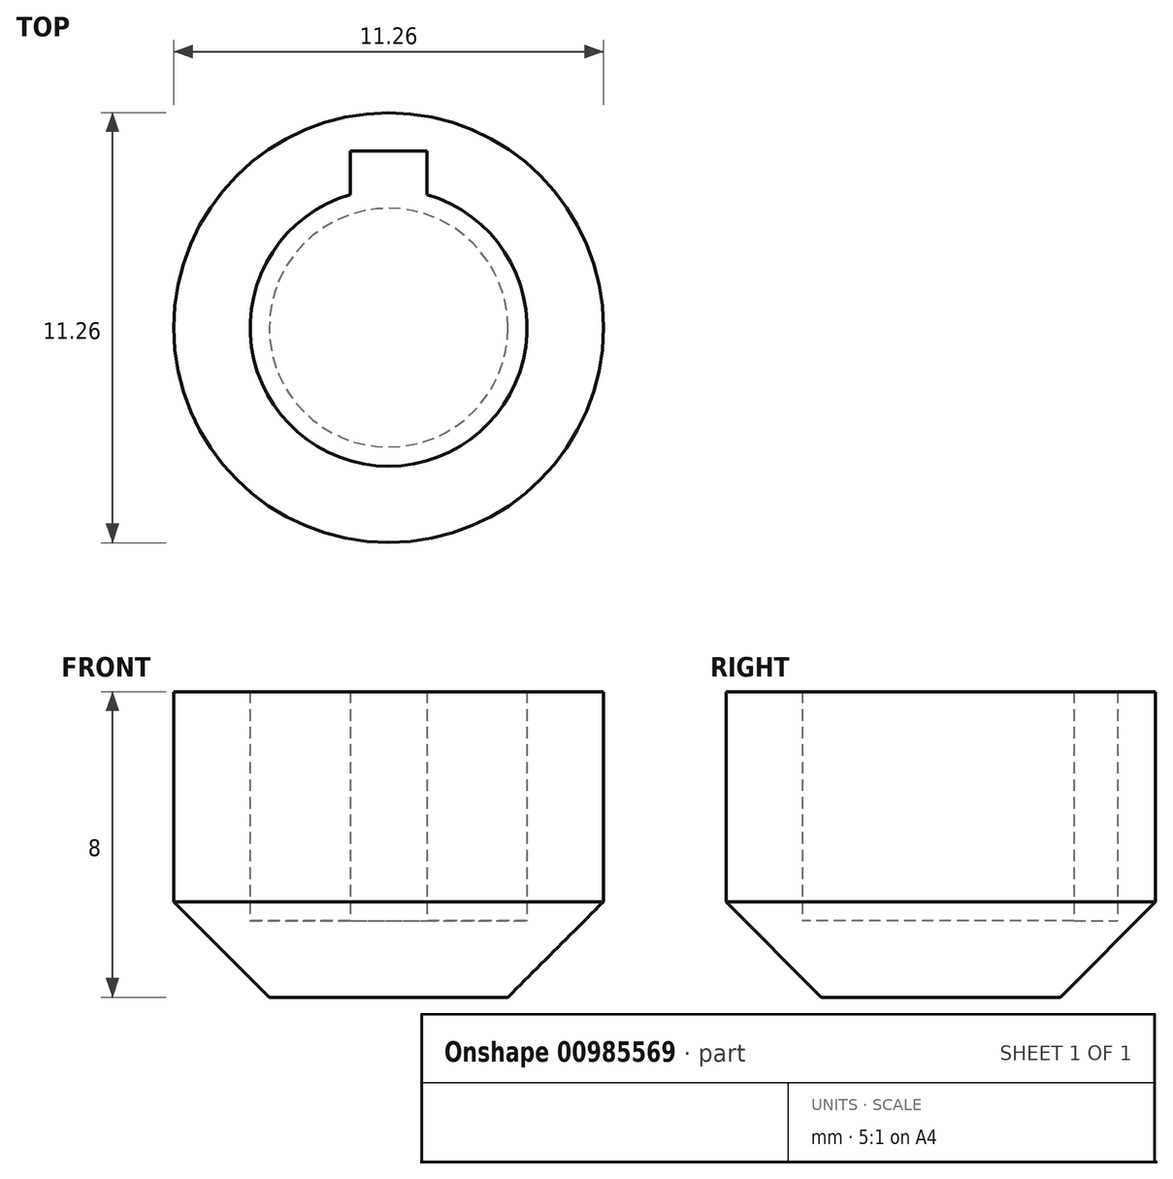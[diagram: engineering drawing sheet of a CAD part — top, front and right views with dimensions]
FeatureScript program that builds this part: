
annotation { "Feature Type Name" : "Feature", "Feature Type Description" : "" }
export const myFeature = defineFeature(function(context is Context, id is Id, definition is map)
    precondition{}
    {
        {
            var Q0;
            Q0=qCreatedBy(makeId("Top.planeOp"),FACE);
            var sketch = newSketch(context, id + "F0", { "sketchPlane" : qUnion([Q0])});
            skCircle(sketch, "E0", {"center": v(0, 0) * mm, "radius": 3.62 * mm});
            skCircle(sketch, "E1", {"center": v(0, 0) * mm, "radius": 5.62 * mm});
            skLineSegment(sketch, "E2.bottom", {"start": v(-1, 2.63) * mm, "end": v(1, 2.63) * mm});
            skLineSegment(sketch, "E2.top", {"start": v(-1, 4.63) * mm, "end": v(1, 4.63) * mm});
            skLineSegment(sketch, "E2.left", {"start": v(-1, 2.63) * mm, "end": v(-1, 4.63) * mm});
            skLineSegment(sketch, "E2.right", {"start": v(1, 2.63) * mm, "end": v(1, 4.63) * mm});
            skPoint(sketch, "E2.middle", {"position": v(0, 3.62) * mm});
            skSolve(sketch);
        }
        {
            var Q0;
            Q0=makeQuery(id+"F0.imprint","IMPRINT",FACE,{"disambiguationData":[TD([[makeQuery(id+"F0.imprint","IMPRINT",EDGE,{"derivedFrom":sQuery(id+"F0.wireOp",EDGE,"E1")}),1.0]])]});
            extrude(context, id + "F1", {"entities" : qUnion([Q0]), "depth" : 8 * mm, "offsetDistance" : 25 * mm});
        }
        {
            var Q0;
            {var subQ5=sQuery(id+"F0.wireOp",EDGE,"E2.bottom");Q0=makeQuery(id+"F0.imprint","IMPRINT",FACE,{"disambiguationData":[TD([[makeQuery(id+"F0.imprint","IMPRINT",EDGE,{"derivedFrom":subQ5}),-1.0]])]});}
            var Q1;
            {var subQ5=sQuery(id+"F0.wireOp",EDGE,"E2.top");Q1=makeQuery(id+"F0.imprint","IMPRINT",FACE,{"disambiguationData":[TD([[makeQuery(id+"F0.imprint","IMPRINT",EDGE,{"derivedFrom":subQ5}),-1.0]])]});}
            var Q2;
            {var subQ5=sQuery(id+"F0.wireOp",EDGE,"E2.bottom");Q2=makeQuery(id+"F0.imprint","IMPRINT",FACE,{"disambiguationData":[TD([[makeQuery(id+"F0.imprint","IMPRINT",EDGE,{"derivedFrom":subQ5}),1.0]])]});}
            extrude(context, id + "F2", {"entities" : qUnion([Q0, Q1, Q2]), "operationType" : NewBodyOperationType.ADD, "depth" : 2 * mm, "offsetDistance" : 25 * mm});
        }
        {
            var Q0;
            Q0=makeQuery(id+"F1.opExtrude","CAP_EDGE",EDGE,{"disambiguationData":[OSD([sQuery(id+"F0.wireOp",EDGE,"E1")])],"isStart":true});
            chamfer(context, id + "F3", {"entities" : qUnion([Q0]), "width" : 2.5 * mm, "tangentPropagation" : true});
        }
    });
